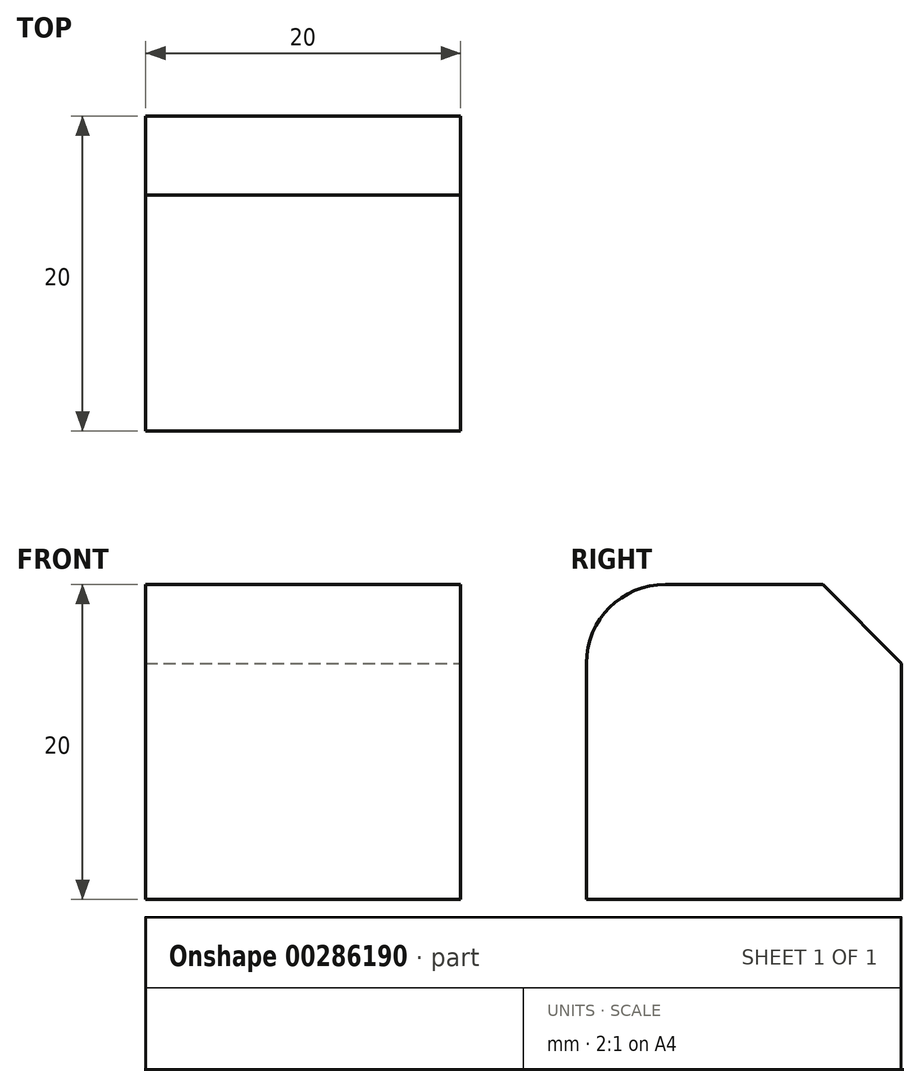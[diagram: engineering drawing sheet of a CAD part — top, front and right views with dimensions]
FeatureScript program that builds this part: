
annotation { "Feature Type Name" : "Feature", "Feature Type Description" : "" }
export const myFeature = defineFeature(function(context is Context, id is Id, definition is map)
    precondition{}
    {
        {
            var Q0;
            Q0=qCreatedBy(makeId("Top.planeOp"),FACE);
            var sketch = newSketch(context, id + "F0", { "sketchPlane" : qUnion([Q0])});
            skLineSegment(sketch, "E0.bottom", {"start": v(-10, 10) * mm, "end": v(10, 10) * mm});
            skLineSegment(sketch, "E0.top", {"start": v(-10, -10) * mm, "end": v(10, -10) * mm});
            skLineSegment(sketch, "E0.left", {"start": v(-10, 10) * mm, "end": v(-10, -10) * mm});
            skLineSegment(sketch, "E0.right", {"start": v(10, 10) * mm, "end": v(10, -10) * mm});
            skPoint(sketch, "E0.middle", {"position": v(0, 0) * mm});
            skSolve(sketch);
        }
        {
            var Q0;
            Q0 = qSketchRegion(id + "F0", true);
            extrude(context, id + "F1", {"entities" : qUnion([Q0]), "depth" : 20 * mm});
        }
        {
            var Q0;
            Q0=makeQuery(id+"F1.opExtrude","CAP_EDGE",EDGE,{"disambiguationData":[OSD([sQuery(id+"F0.wireOp",EDGE,"E0.bottom")])],"isStart":false});
            chamfer(context, id + "F2", {"entities" : qUnion([Q0]), "width" : 5 * mm, "tangentPropagation" : true});
        }
        {
            var Q0;
            Q0=makeQuery(id+"F1.opExtrude","CAP_EDGE",EDGE,{"disambiguationData":[OSD([sQuery(id+"F0.wireOp",EDGE,"E0.top")])],"isStart":false});
            fillet(context, id + "F3", {"entities" : qUnion([Q0]), "radius" : 5 * mm, "tangentPropagation" : true, "allowEdgeOverflow" : false});
        }
    });
